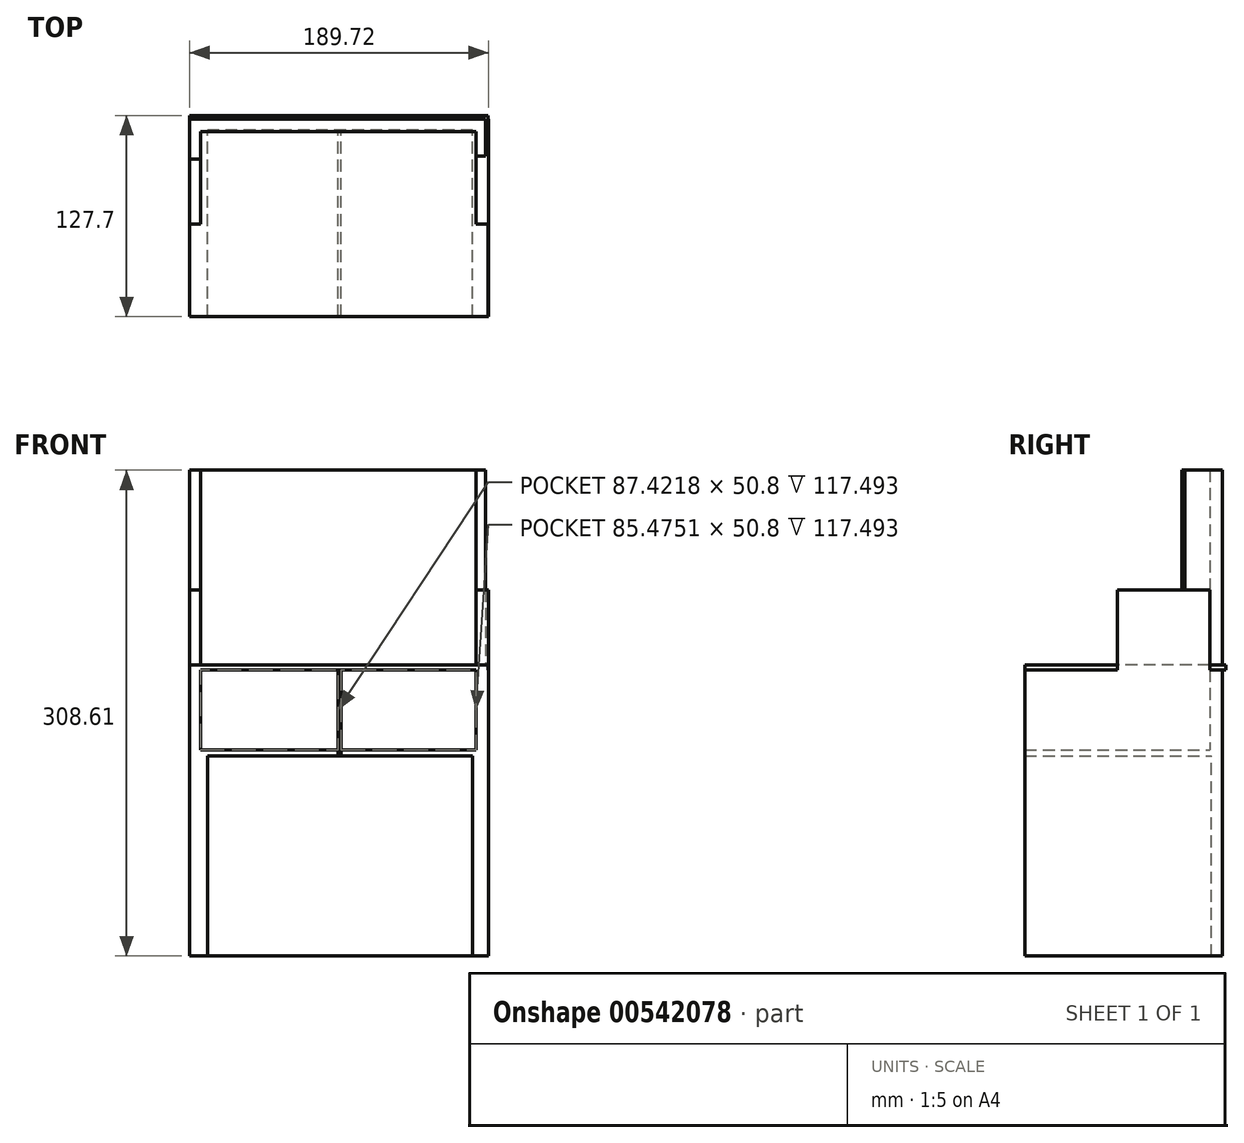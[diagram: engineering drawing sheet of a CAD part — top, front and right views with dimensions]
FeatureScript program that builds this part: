
annotation { "Feature Type Name" : "Feature", "Feature Type Description" : "" }
export const myFeature = defineFeature(function(context is Context, id is Id, definition is map)
    precondition{}
    {
        {
            var Q0;
            Q0=qCreatedBy(makeId("Top.planeOp"),FACE);
            var sketch = newSketch(context, id + "F0", { "sketchPlane" : qUnion([Q0])});
            skLineSegment(sketch, "E0.bottom", {"start": v(-125.77, -10.21) * mm, "end": v(63.95, -10.21) * mm});
            skLineSegment(sketch, "E0.top", {"start": v(-125.77, 115.13) * mm, "end": v(63.95, 115.13) * mm});
            skLineSegment(sketch, "E0.left", {"start": v(-125.77, -10.21) * mm, "end": v(-125.77, 115.13) * mm});
            skLineSegment(sketch, "E0.right", {"start": v(63.95, -10.21) * mm, "end": v(63.95, 115.13) * mm});
            skSolve(sketch);
        }
        {
            var Q0;
            Q0 = qSketchRegion(id + "F0", true);
            extrude(context, id + "F1", {"entities" : qUnion([Q0]), "depth" : 3.8 * mm, "offsetDistance" : 25.4 * mm});
        }
        {
            var Q0;
            Q0=makeQuery(id+"F1.opExtrude","CAP_FACE",FACE,{"disambiguationData":[OSD([sQuery(id+"F0.wireOp",EDGE,"E0.bottom"),sQuery(id+"F0.wireOp",EDGE,"E0.top"),sQuery(id+"F0.wireOp",EDGE,"E0.left"),sQuery(id+"F0.wireOp",EDGE,"E0.right")])],"isStart":false});
            var sketch = newSketch(context, id + "F2", { "sketchPlane" : qUnion([Q0])});
            skLineSegment(sketch, "E1.bottom", {"start": v(-118.83, 115.13) * mm, "end": v(-125.77, 115.13) * mm});
            skLineSegment(sketch, "E1.top", {"start": v(-118.83, -10.21) * mm, "end": v(-125.77, -10.21) * mm});
            skLineSegment(sketch, "E1.left", {"start": v(-118.83, 115.13) * mm, "end": v(-118.83, -10.21) * mm});
            skLineSegment(sketch, "E1.right", {"start": v(-125.77, 115.13) * mm, "end": v(-125.77, -10.21) * mm});
            skSolve(sketch);
        }
        {
            var Q0;
            Q0 = qSketchRegion(id + "F2", true);
            extrude(context, id + "F3", {"entities" : qUnion([Q0]), "operationType" : NewBodyOperationType.ADD, "depth" : 50.8 * mm, "offsetDistance" : 25.4 * mm});
        }
        {
            var Q0;
            Q0=makeQuery(id+"F1.opExtrude","CAP_FACE",FACE,{"disambiguationData":[OSD([sQuery(id+"F0.wireOp",EDGE,"E0.bottom"),sQuery(id+"F0.wireOp",EDGE,"E0.top"),sQuery(id+"F0.wireOp",EDGE,"E0.left"),sQuery(id+"F0.wireOp",EDGE,"E0.right")])],"isStart":false});
            var sketch = newSketch(context, id + "F4", { "sketchPlane" : qUnion([Q0])});
            skLineSegment(sketch, "E2.bottom", {"start": v(56, 115.13) * mm, "end": v(63.95, 115.13) * mm});
            skLineSegment(sketch, "E2.top", {"start": v(56, -10.21) * mm, "end": v(63.95, -10.21) * mm});
            skLineSegment(sketch, "E2.left", {"start": v(56, 115.13) * mm, "end": v(56, -10.21) * mm});
            skLineSegment(sketch, "E2.right", {"start": v(63.95, 115.13) * mm, "end": v(63.95, -10.21) * mm});
            skSolve(sketch);
        }
        {
            var Q0;
            Q0 = qSketchRegion(id + "F4", true);
            extrude(context, id + "F5", {"entities" : qUnion([Q0]), "operationType" : NewBodyOperationType.ADD, "depth" : 50.8 * mm, "offsetDistance" : 25.4 * mm});
        }
        {
            var Q0;
            Q0=makeQuery(id+"F1.opExtrude","CAP_FACE",FACE,{"disambiguationData":[OSD([sQuery(id+"F0.wireOp",EDGE,"E0.bottom"),sQuery(id+"F0.wireOp",EDGE,"E0.top"),sQuery(id+"F0.wireOp",EDGE,"E0.left"),sQuery(id+"F0.wireOp",EDGE,"E0.right")])],"isStart":false});
            var sketch = newSketch(context, id + "F6", { "sketchPlane" : qUnion([Q0])});
            skLineSegment(sketch, "E3.bottom", {"start": v(-118.83, 115.13) * mm, "end": v(62.19, 115.13) * mm});
            skLineSegment(sketch, "E3.top", {"start": v(-118.83, 107.28) * mm, "end": v(62.19, 107.28) * mm});
            skLineSegment(sketch, "E3.left", {"start": v(-118.83, 115.13) * mm, "end": v(-118.83, 107.28) * mm});
            skLineSegment(sketch, "E3.right", {"start": v(62.19, 115.13) * mm, "end": v(62.19, 107.28) * mm});
            skSolve(sketch);
        }
        {
            var Q0;
            Q0 = qSketchRegion(id + "F6", true);
            extrude(context, id + "F7", {"entities" : qUnion([Q0]), "operationType" : NewBodyOperationType.ADD, "depth" : 177.8 * mm, "offsetDistance" : 25.4 * mm});
        }
        {
            var Q0;
            Q0=makeQuery(id+"F3.opExtrude","CAP_FACE",FACE,{"disambiguationData":[OSD([sQuery(id+"F2.wireOp",EDGE,"E1.bottom"),sQuery(id+"F2.wireOp",EDGE,"E1.top"),sQuery(id+"F2.wireOp",EDGE,"E1.left"),sQuery(id+"F2.wireOp",EDGE,"E1.right")])],"isStart":false});
            var sketch = newSketch(context, id + "F8", { "sketchPlane" : qUnion([Q0])});
            skPoint(sketch, "E4.oppositeSnap0", {"position": v(-118.83, 48.53) * mm});
            skLineSegment(sketch, "E4.bottom", {"start": v(-118.83, 115.13) * mm, "end": v(-125.77, 115.13) * mm});
            skLineSegment(sketch, "E4.top", {"start": v(-118.83, 48.53) * mm, "end": v(-125.77, 48.53) * mm});
            skLineSegment(sketch, "E4.left", {"start": v(-118.83, 115.13) * mm, "end": v(-118.83, 48.53) * mm});
            skLineSegment(sketch, "E4.right", {"start": v(-125.77, 115.13) * mm, "end": v(-125.77, 48.53) * mm});
            skSolve(sketch);
        }
        {
            var Q0;
            Q0 = qSketchRegion(id + "F8", true);
            extrude(context, id + "F9", {"entities" : qUnion([Q0]), "operationType" : NewBodyOperationType.ADD, "depth" : 50.8 * mm, "offsetDistance" : 25.4 * mm});
        }
        {
            var Q0;
            Q0=makeQuery(id+"F9.opExtrude","CAP_FACE",FACE,{"disambiguationData":[OSD([sQuery(id+"F8.wireOp",EDGE,"E4.bottom"),sQuery(id+"F8.wireOp",EDGE,"E4.top"),sQuery(id+"F8.wireOp",EDGE,"E4.left"),sQuery(id+"F8.wireOp",EDGE,"E4.right")])],"isStart":false});
            var sketch = newSketch(context, id + "F10", { "sketchPlane" : qUnion([Q0])});
            skLineSegment(sketch, "E5.bottom", {"start": v(-125.77, 115.13) * mm, "end": v(-118.83, 115.13) * mm});
            skLineSegment(sketch, "E5.top", {"start": v(-125.77, 89.6) * mm, "end": v(-118.83, 89.6) * mm});
            skLineSegment(sketch, "E5.left", {"start": v(-125.77, 115.13) * mm, "end": v(-125.77, 89.6) * mm});
            skLineSegment(sketch, "E5.right", {"start": v(-118.83, 115.13) * mm, "end": v(-118.83, 89.6) * mm});
            skSolve(sketch);
        }
        {
            var Q0;
            Q0 = qSketchRegion(id + "F10", true);
            extrude(context, id + "F11", {"entities" : qUnion([Q0]), "operationType" : NewBodyOperationType.ADD, "depth" : 76.2 * mm, "offsetDistance" : 25.4 * mm});
        }
        {
            var Q0;
            Q0=makeQuery(id+"F5.opExtrude","CAP_FACE",FACE,{"disambiguationData":[OSD([sQuery(id+"F4.wireOp",EDGE,"E2.bottom"),sQuery(id+"F4.wireOp",EDGE,"E2.top"),sQuery(id+"F4.wireOp",EDGE,"E2.left"),sQuery(id+"F4.wireOp",EDGE,"E2.right")])],"isStart":false});
            var sketch = newSketch(context, id + "F12", { "sketchPlane" : qUnion([Q0])});
            skPoint(sketch, "E6.oppositeSnap0", {"position": v(56, 48.53) * mm});
            skLineSegment(sketch, "E6.bottom", {"start": v(56, 107.28) * mm, "end": v(63.95, 107.28) * mm});
            skLineSegment(sketch, "E6.top", {"start": v(56, 48.53) * mm, "end": v(63.95, 48.53) * mm});
            skLineSegment(sketch, "E6.left", {"start": v(56, 107.28) * mm, "end": v(56, 48.53) * mm});
            skLineSegment(sketch, "E6.right", {"start": v(63.95, 107.28) * mm, "end": v(63.95, 48.53) * mm});
            skSolve(sketch);
        }
        {
            var Q0;
            Q0 = qSketchRegion(id + "F12", true);
            extrude(context, id + "F13", {"entities" : qUnion([Q0]), "operationType" : NewBodyOperationType.ADD, "depth" : 50.8 * mm, "offsetDistance" : 25.4 * mm});
        }
        {
            var Q0;
            Q0=makeQuery(id+"F13.opExtrude","CAP_FACE",FACE,{"disambiguationData":[OSD([sQuery(id+"F12.wireOp",EDGE,"E6.bottom"),sQuery(id+"F12.wireOp",EDGE,"E6.top"),sQuery(id+"F12.wireOp",EDGE,"E6.left"),sQuery(id+"F12.wireOp",EDGE,"E6.right")])],"isStart":false});
            var sketch = newSketch(context, id + "F14", { "sketchPlane" : qUnion([Q0])});
            skLineSegment(sketch, "E7.bottom", {"start": v(62.19, 107.28) * mm, "end": v(56, 107.28) * mm});
            skLineSegment(sketch, "E7.top", {"start": v(62.19, 91.52) * mm, "end": v(56, 91.52) * mm});
            skLineSegment(sketch, "E7.left", {"start": v(62.19, 107.28) * mm, "end": v(62.19, 91.52) * mm});
            skLineSegment(sketch, "E7.right", {"start": v(56, 107.28) * mm, "end": v(56, 91.52) * mm});
            skSolve(sketch);
        }
        {
            var Q0;
            Q0 = qSketchRegion(id + "F14", true);
            extrude(context, id + "F15", {"entities" : qUnion([Q0]), "operationType" : NewBodyOperationType.ADD, "depth" : 76.2 * mm, "offsetDistance" : 25.4 * mm});
        }
        {
            var Q0;
            Q0=makeQuery(id+"F3.opExtrude","CAP_FACE",FACE,{"disambiguationData":[OSD([sQuery(id+"F2.wireOp",EDGE,"E1.bottom"),sQuery(id+"F2.wireOp",EDGE,"E1.top"),sQuery(id+"F2.wireOp",EDGE,"E1.left"),sQuery(id+"F2.wireOp",EDGE,"E1.right")])],"isStart":false});
            var sketch = newSketch(context, id + "F16", { "sketchPlane" : qUnion([Q0])});
            skLineSegment(sketch, "E8.bottom", {"start": v(-125.77, -10.21) * mm, "end": v(63.84, -10.21) * mm});
            skLineSegment(sketch, "E8.top", {"start": v(-125.77, 117.38) * mm, "end": v(63.84, 117.38) * mm});
            skLineSegment(sketch, "E8.left", {"start": v(-125.77, -10.21) * mm, "end": v(-125.77, 117.38) * mm});
            skLineSegment(sketch, "E8.right", {"start": v(63.84, -10.21) * mm, "end": v(63.84, 117.38) * mm});
            skSolve(sketch);
        }
        {
            var Q0;
            Q0 = qSketchRegion(id + "F16", true);
            extrude(context, id + "F17", {"entities" : qUnion([Q0]), "operationType" : NewBodyOperationType.ADD, "depth" : 3.3 * mm, "offsetDistance" : 25.4 * mm});
        }
        {
            var Q0;
            Q0=makeQuery(id+"F17.boolean.opBoolean","SPLIT",FACE,{"disambiguationData":[TD([makeQuery(id+"F1.opExtrude","CAP_FACE",FACE,{"disambiguationData":[OSD([sQuery(id+"F0.wireOp",EDGE,"E0.bottom"),sQuery(id+"F0.wireOp",EDGE,"E0.top"),sQuery(id+"F0.wireOp",EDGE,"E0.left"),sQuery(id+"F0.wireOp",EDGE,"E0.right")])],"isStart":false})])],"derivedFrom":makeQuery(id+"F7.opExtrude","SWEPT_FACE",FACE,{"disambiguationData":[OSD([sQuery(id+"F6.wireOp",EDGE,"E3.top")])]})});
            var sketch = newSketch(context, id + "F18", { "sketchPlane" : qUnion([Q0])});
            skLineSegment(sketch, "E9.bottom", {"start": v(-31.41, 54.61) * mm, "end": v(-29.47, 54.61) * mm});
            skLineSegment(sketch, "E9.top", {"start": v(-31.41, 0) * mm, "end": v(-29.47, 0) * mm});
            skLineSegment(sketch, "E9.left", {"start": v(-31.41, 54.61) * mm, "end": v(-31.41, 0) * mm});
            skLineSegment(sketch, "E9.right", {"start": v(-29.47, 54.61) * mm, "end": v(-29.47, 0) * mm});
            skSolve(sketch);
        }
        {
            var Q0;
            Q0 = qSketchRegion(id + "F18", true);
            extrude(context, id + "F19", {"entities" : qUnion([Q0]), "operationType" : NewBodyOperationType.ADD, "depth" : 117.6 * mm, "offsetDistance" : 25.4 * mm});
        }
        {
            var Q0;
            Q0=makeQuery(id+"F19.boolean.opBoolean","MERGE",FACE,{"derivedFrom":[makeQuery(id+"F1.opExtrude","CAP_FACE",FACE,{"disambiguationData":[OSD([sQuery(id+"F0.wireOp",EDGE,"E0.bottom"),sQuery(id+"F0.wireOp",EDGE,"E0.top"),sQuery(id+"F0.wireOp",EDGE,"E0.left"),sQuery(id+"F0.wireOp",EDGE,"E0.right")])],"isStart":true}),makeQuery(id+"F19.opExtrude","SWEPT_FACE",FACE,{"disambiguationData":[OSD([sQuery(id+"F18.wireOp",EDGE,"E9.top")])]})]});
            var sketch = newSketch(context, id + "F20", { "sketchPlane" : qUnion([Q0])});
            skLineSegment(sketch, "E10.bottom", {"start": v(-114.26, 10.21) * mm, "end": v(-125.77, 10.21) * mm});
            skLineSegment(sketch, "E10.top", {"start": v(-114.26, -115.13) * mm, "end": v(-125.77, -115.13) * mm});
            skLineSegment(sketch, "E10.left", {"start": v(-114.26, 10.21) * mm, "end": v(-114.26, -115.13) * mm});
            skLineSegment(sketch, "E10.right", {"start": v(-125.77, 10.21) * mm, "end": v(-125.77, -115.13) * mm});
            skSolve(sketch);
        }
        {
            var Q0;
            Q0 = qSketchRegion(id + "F20", true);
            extrude(context, id + "F21", {"entities" : qUnion([Q0]), "operationType" : NewBodyOperationType.ADD, "depth" : 127 * mm, "offsetDistance" : 25.4 * mm});
        }
        {
            var Q0;
            Q0=makeQuery(id+"F19.boolean.opBoolean","MERGE",FACE,{"derivedFrom":[makeQuery(id+"F1.opExtrude","CAP_FACE",FACE,{"disambiguationData":[OSD([sQuery(id+"F0.wireOp",EDGE,"E0.bottom"),sQuery(id+"F0.wireOp",EDGE,"E0.top"),sQuery(id+"F0.wireOp",EDGE,"E0.left"),sQuery(id+"F0.wireOp",EDGE,"E0.right")])],"isStart":true}),makeQuery(id+"F19.opExtrude","SWEPT_FACE",FACE,{"disambiguationData":[OSD([sQuery(id+"F18.wireOp",EDGE,"E9.top")])]})]});
            var sketch = newSketch(context, id + "F22", { "sketchPlane" : qUnion([Q0])});
            skLineSegment(sketch, "E11.bottom", {"start": v(53.95, 10.21) * mm, "end": v(63.95, 10.21) * mm});
            skLineSegment(sketch, "E11.top", {"start": v(53.95, -115.13) * mm, "end": v(63.95, -115.13) * mm});
            skLineSegment(sketch, "E11.left", {"start": v(53.95, 10.21) * mm, "end": v(53.95, -115.13) * mm});
            skLineSegment(sketch, "E11.right", {"start": v(63.95, 10.21) * mm, "end": v(63.95, -115.13) * mm});
            skSolve(sketch);
        }
        {
            var Q0;
            Q0 = qSketchRegion(id + "F22", true);
            extrude(context, id + "F23", {"entities" : qUnion([Q0]), "operationType" : NewBodyOperationType.ADD, "depth" : 127 * mm, "offsetDistance" : 25.4 * mm});
        }
        {
            var Q0;
            Q0=makeQuery(id+"F19.boolean.opBoolean","MERGE",FACE,{"derivedFrom":[makeQuery(id+"F1.opExtrude","CAP_FACE",FACE,{"disambiguationData":[OSD([sQuery(id+"F0.wireOp",EDGE,"E0.bottom"),sQuery(id+"F0.wireOp",EDGE,"E0.top"),sQuery(id+"F0.wireOp",EDGE,"E0.left"),sQuery(id+"F0.wireOp",EDGE,"E0.right")])],"isStart":true}),makeQuery(id+"F19.opExtrude","SWEPT_FACE",FACE,{"disambiguationData":[OSD([sQuery(id+"F18.wireOp",EDGE,"E9.top")])]})]});
            var sketch = newSketch(context, id + "F24", { "sketchPlane" : qUnion([Q0])});
            skLineSegment(sketch, "E12.bottom", {"start": v(53.95, -115.13) * mm, "end": v(-124.86, -115.13) * mm});
            skLineSegment(sketch, "E12.top", {"start": v(53.95, -108.15) * mm, "end": v(-124.86, -108.15) * mm});
            skLineSegment(sketch, "E12.left", {"start": v(53.95, -115.13) * mm, "end": v(53.95, -108.15) * mm});
            skLineSegment(sketch, "E12.right", {"start": v(-124.86, -115.13) * mm, "end": v(-124.86, -108.15) * mm});
            skSolve(sketch);
        }
        {
            var Q0;
            Q0 = qSketchRegion(id + "F24", true);
            extrude(context, id + "F25", {"entities" : qUnion([Q0]), "operationType" : NewBodyOperationType.ADD, "depth" : 127 * mm, "offsetDistance" : 25.4 * mm});
        }
    });
